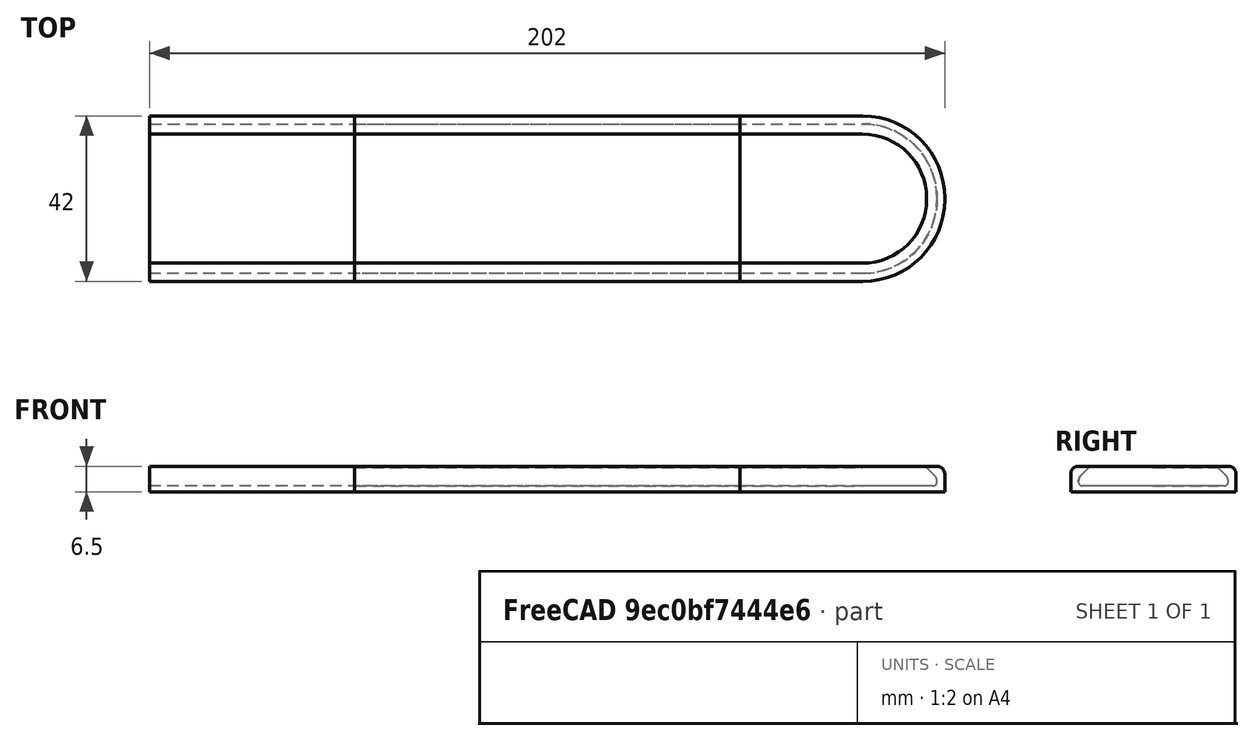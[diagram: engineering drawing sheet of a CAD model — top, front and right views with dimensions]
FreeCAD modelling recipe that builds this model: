
FCSTD DOCUMENT  (FreeCAD 0.19R24276 (Git))
Label: Nespresso
License: All rights reserved
LicenseURL: http://en.wikipedia.org/wiki/All_rights_reserved
objects: Part::Fillet×5, Part::Box×3, Part::Feature×3, Part::MultiFuse×2, Part::Cut×2, Part::Chamfer×1
note: 16 computed .brp shape members not serialized (recipe doc carries the construction recipe); baked Part::Feature solids carry a one-line shape summary decoded from their .brp

FEATURE [Part::Box] Box  label="Hollow"
  AttacherType = Attacher::AttachEngine3D
  Height = 5.1
  Length = 200
  Placement = pos=(0,0,1.5) rot=(0,0,1;0rad)
  Width = 38
FEATURE [Part::Box] Box001  label="Cube001"
  AttacherType = Attacher::AttachEngine3D
  Height = 6.5
  Length = 150
  Placement = pos=(0,-2,0) rot=(0,0,1;0rad)
  Width = 42
FEATURE [Part::Fillet] Fillet
  Base = -> Box
  Edges = 2 edges r=18.8: [Edge5,Edge7]
FEATURE [Part::Chamfer] Chamfer
  Base = -> Fillet
  Edges = 1 edges r=3: [Edge8]
FEATURE [Part::Fillet] Fillet001
  Base = -> Chamfer
  Edges = 1 edges r=1: [Edge7]
FEATURE [Part::Fillet] Fillet002  label="CapsuleHollow"
  Base = -> Fillet001
  Edges = 1 edges r=2: [Edge6]
FEATURE [Part::Box] Box003  label="Hollow002"
  AttacherType = Attacher::AttachEngine3D
  Height = 5.1
  Length = 200
  Placement = pos=(-2.6,2.6,1.5) rot=(0,0,1;0rad)
  Width = 32.8
FEATURE [Part::Fillet] Fillet002004  label="Cutout"
  Base = -> Box003
  Edges = 2 edges r=16.3: [Edge5,Edge7]
FEATURE [Part::Feature] Fillet002004001  label="Cutout001"
  shape: bbox 200 x 32.8 x 5.1 mm, 8 faces (baked)
FEATURE [Part::Feature] Fillet002003001  label="OuterBox"
  shape: bbox 151.7 x 45.43 x 6.5 mm, 13 faces (baked)
FEATURE [Part::Feature] Fillet002004002  label="CapsuleHollow001"
  shape: bbox 201.5 x 41.1 x 5.1 mm, 23 faces (baked)
FEATURE [Part::MultiFuse] Fusion
  Shapes = -> [Fillet002004001,Fillet002004002]
FEATURE [Part::Cut] Cut001  label="CapsuleHolder_001"
  Base = -> Fillet002003001
  Tool = -> Fusion
FEATURE [Part::Fillet] Fillet002004003  label="Box"
  Base = -> Box001
  Edges = 2 edges r=2: [Edge10,Edge12]
FEATURE [Part::MultiFuse] Fusion001
  Shapes = -> [Fillet002,Fillet002004]
FEATURE [Part::Cut] Cut  label="CapsuleHolder_002"
  Base = -> Fillet002004003
  Tool = -> Fusion001
